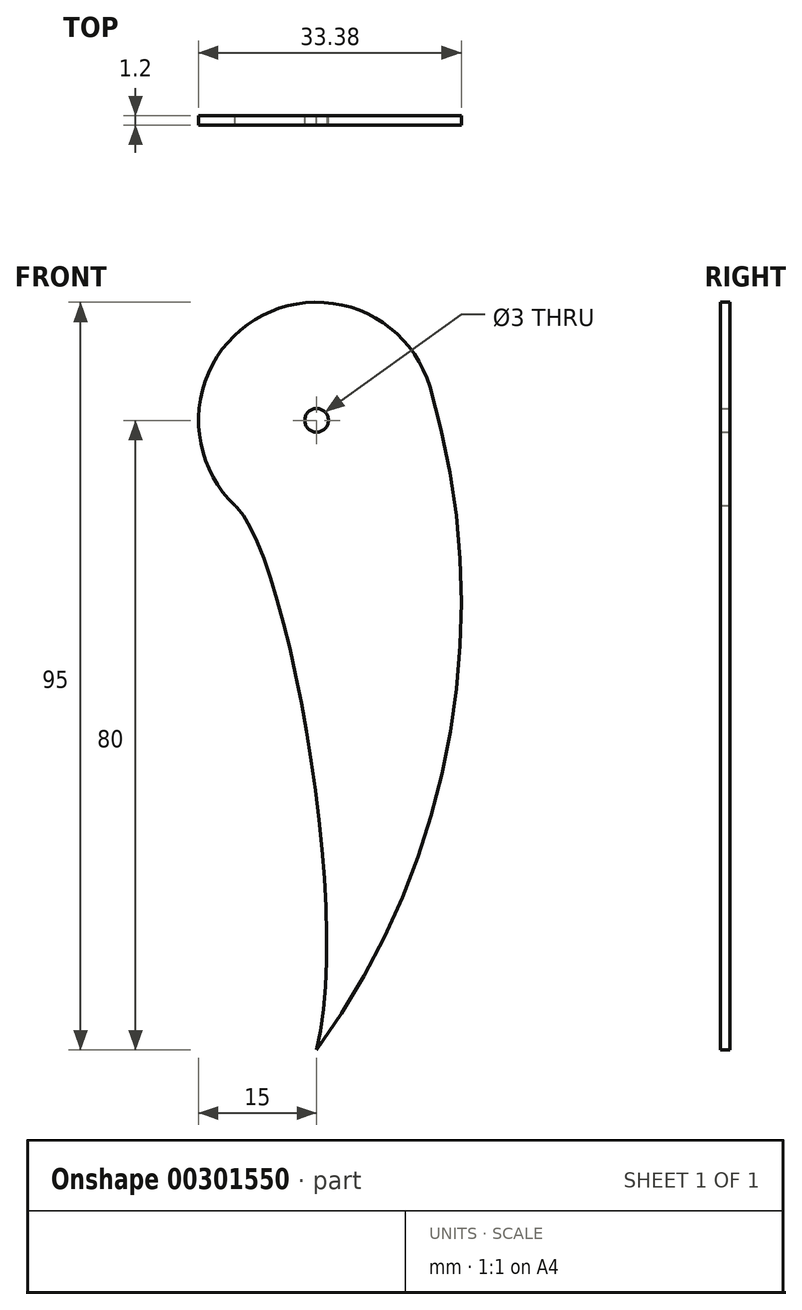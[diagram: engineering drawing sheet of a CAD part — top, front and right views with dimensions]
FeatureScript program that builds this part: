
annotation { "Feature Type Name" : "Feature", "Feature Type Description" : "" }
export const myFeature = defineFeature(function(context is Context, id is Id, definition is map)
    precondition{}
    {
        {
            var Q0;
            Q0=qCreatedBy(makeId("Front.planeOp"),FACE);
            var sketch = newSketch(context, id + "F0", { "sketchPlane" : qUnion([Q0])});
            skCircle(sketch, "E0", {"center": v(0, 0) * mm, "radius": 15 * mm});
            skFitSpline(sketch, "E1", {"points": [v(0, -80) * mm, v(-10.37, -10.84) * mm], "startDerivative": vector(13.77, 53.33) * mm, "endDerivative": vector(-19.18, 16.46) * mm});
            skCircle(sketch, "E2", {"center": v(0, 0) * mm, "radius": 1.5 * mm});
            skArc(sketch, "E3", {"start": v(0, -80) * mm, "mid": v(17, -39.54) * mm, "end": v(14.38, 4.27) * mm});
            skSolve(sketch);
        }
        {
            var Q0;
            {var subQ0=sQuery(id+"F0.wireOp",EDGE,"E0");var subQ1=makeQuery(id+"F0.imprint","INTERSECT",VERTEX,{"derivedFrom":[subQ0,sQuery(id+"F0.wireOp",EDGE,"r6FlJ5GV-F9nt-dUkj-J55f-k1Xnp1ZBbLi6")]});Q0=makeQuery(id+"F0.imprint","IMPRINT",FACE,{"disambiguationData":[TD([[makeQuery(id+"F0.imprint","IMPRINT",EDGE,{"disambiguationData":[TD([[subQ1,1.0]])],"derivedFrom":subQ0}),1.0]])]});}
            var Q1;
            {var subQ0=sQuery(id+"F0.wireOp",EDGE,"E3");Q1=makeQuery(id+"F0.imprint","IMPRINT",FACE,{"disambiguationData":[TD([[makeQuery(id+"F0.imprint","IMPRINT",EDGE,{"derivedFrom":subQ0}),1.0]])]});}
            extrude(context, id + "F1", {"entities" : qUnion([Q0, Q1]), "depth" : 1.2 * mm});
        }
    });
